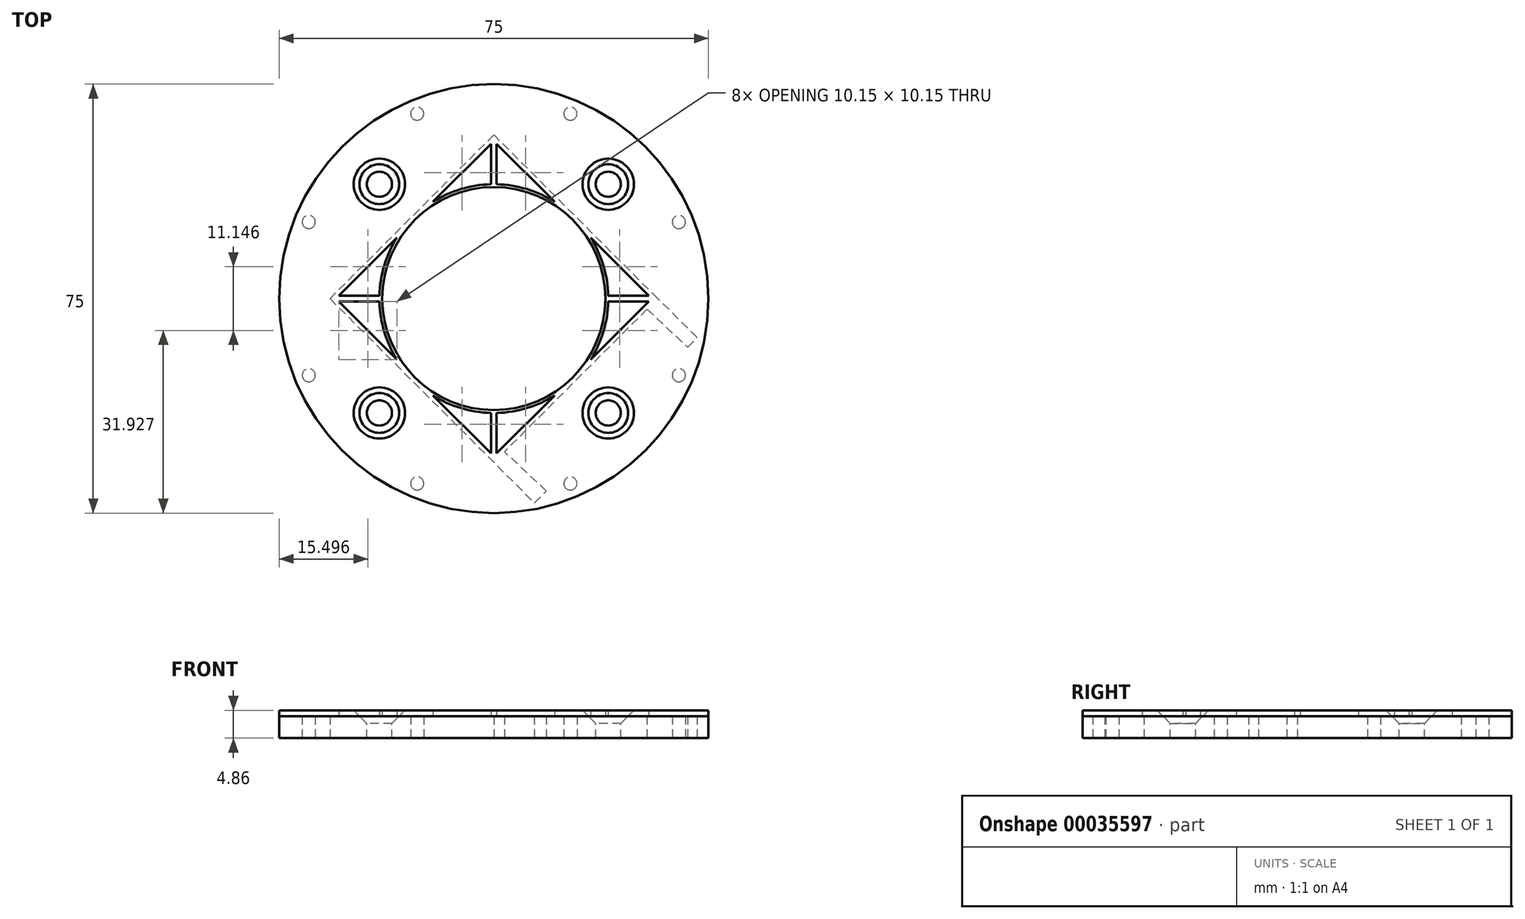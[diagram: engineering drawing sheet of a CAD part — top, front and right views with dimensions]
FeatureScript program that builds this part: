
annotation { "Feature Type Name" : "Feature", "Feature Type Description" : "" }
export const myFeature = defineFeature(function(context is Context, id is Id, definition is map)
    precondition{}
    {
        {
            var Q0;
            Q0=qCreatedBy(makeId("Top.planeOp"),FACE);
            var sketch = newSketch(context, id + "F0", { "sketchPlane" : qUnion([Q0])});
            skLineSegment(sketch, "E0.rect.bottom", {"start": v(20, -20) * mm, "end": v(-20, -20) * mm, "construction": true});
            skLineSegment(sketch, "E0.rect.top", {"start": v(20, 20) * mm, "end": v(-20, 20) * mm, "construction": true});
            skLineSegment(sketch, "E0.rect.left", {"start": v(20, -20) * mm, "end": v(20, 20) * mm, "construction": true});
            skPoint(sketch, "E0.rect.middle", {"position": v(0, 0) * mm});
            skLineSegment(sketch, "E1.bottom", {"start": v(26.79, -1.85) * mm, "end": v(1.86, -26.78) * mm});
            skLineSegment(sketch, "E1.left", {"start": v(28.64, 0) * mm, "end": v(0, 28.64) * mm});
            skLineSegment(sketch, "E1.right", {"start": v(0, -28.64) * mm, "end": v(-28.64, 0) * mm});
            skLineSegment(sketch, "E2", {"start": v(0, 28.64) * mm, "end": v(-28.64, 0) * mm});
            skCircle(sketch, "E3", {"center": v(0, 0) * mm, "radius": 37.5 * mm});
            skLineSegment(sketch, "E4", {"start": v(0, -28.64) * mm, "end": v(7.09, -35.72) * mm});
            skLineSegment(sketch, "E5", {"start": v(7.09, -35.72) * mm, "end": v(9.18, -33.63) * mm});
            skLineSegment(sketch, "E6", {"start": v(9.18, -33.63) * mm, "end": v(1.86, -26.78) * mm});
            skLineSegment(sketch, "E7", {"start": v(26.79, -1.85) * mm, "end": v(33.9, -8.51) * mm});
            skLineSegment(sketch, "E8", {"start": v(33.9, -8.51) * mm, "end": v(35.53, -6.77) * mm});
            skLineSegment(sketch, "E9", {"start": v(35.53, -6.77) * mm, "end": v(28.64, 0) * mm});
            skArc(sketch, "E10", {"start": v(6.24, -30.88) * mm, "mid": v(22.44, -22.1) * mm, "end": v(30.97, -5.77) * mm});
            skArc(sketch, "E11.trimOffspring", {"start": v(31.38, -2.7) * mm, "mid": v(-22.29, 22.26) * mm, "end": v(2.74, -31.38) * mm});
            skLineSegment(sketch, "E12", {"start": v(-20, -20) * mm, "end": v(-20, 20) * mm, "construction": true});
            skArc(sketch, "E13", {"start": v(5.87, -34.5) * mm, "mid": v(24.78, -24.72) * mm, "end": v(34.52, -5.78) * mm});
            skLineSegment(sketch, "E14", {"start": v(0, 0) * mm, "end": v(-40.64, 0) * mm, "construction": true});
            skLineSegment(sketch, "E15", {"start": v(-40.64, 0) * mm, "end": v(40.13, 0) * mm, "construction": true});
            skLineSegment(sketch, "E16", {"start": v(0, 0) * mm, "end": v(0, 39.12) * mm, "construction": true});
            skLineSegment(sketch, "E17", {"start": v(0, 0) * mm, "end": v(0, -39.38) * mm, "construction": true});
            skLineSegment(sketch, "E18", {"start": v(0, -39.38) * mm, "end": v(0, 0) * mm, "construction": true});
            skLineSegment(sketch, "E19", {"start": v(0, 0) * mm, "end": v(-39.64, 16.42) * mm, "construction": true});
            skLineSegment(sketch, "E20", {"start": v(0, 0) * mm, "end": v(-16.12, 38.93) * mm, "construction": true});
            skLineSegment(sketch, "E21", {"start": v(0, 0) * mm, "end": v(15.42, 37.24) * mm, "construction": true});
            skLineSegment(sketch, "E22", {"start": v(0, 0) * mm, "end": v(38.4, 15.9) * mm, "construction": true});
            skLineSegment(sketch, "E23", {"start": v(0, 0) * mm, "end": v(-37.76, -15.64) * mm, "construction": true});
            skLineSegment(sketch, "E24", {"start": v(0, 0) * mm, "end": v(-15.38, -37.13) * mm, "construction": true});
            skLineSegment(sketch, "E25", {"start": v(0, 0) * mm, "end": v(17.57, -42.41) * mm, "construction": true});
            skLineSegment(sketch, "E26", {"start": v(0, 0) * mm, "end": v(48.8, -20.21) * mm, "construction": true});
            skCircle(sketch, "E27", {"center": v(0, 0) * mm, "radius": 35 * mm, "construction": true});
            skPoint(sketch, "E28", {"position": v(-32.34, 13.4) * mm});
            skPoint(sketch, "E29", {"position": v(-13.4, 32.34) * mm});
            skPoint(sketch, "E30", {"position": v(13.4, 32.34) * mm});
            skPoint(sketch, "E31", {"position": v(32.34, 13.4) * mm});
            skPoint(sketch, "E32", {"position": v(32.34, -13.4) * mm});
            skPoint(sketch, "E33", {"position": v(13.4, -32.34) * mm});
            skPoint(sketch, "E34", {"position": v(-13.4, -32.34) * mm});
            skPoint(sketch, "E35", {"position": v(-32.34, -13.4) * mm});
            skSolve(sketch);
        }
        {
            var Q0;
            {var subQ1=sQuery(id+"F0.wireOp",EDGE,"63a967cb-fa63-414c-9bd4-498ef804fca7");Q0=makeQuery(id+"F0.imprint","IMPRINT",FACE,{"disambiguationData":[TD([[makeQuery(id+"F0.imprint","IMPRINT",EDGE,{"derivedFrom":subQ1}),1.0]])]});}
            var Q1;
            Q1=makeQuery(id+"F0.imprint","IMPRINT",FACE,{"disambiguationData":[TD([[makeQuery(id+"F0.imprint","IMPRINT",EDGE,{"derivedFrom":sQuery(id+"F0.wireOp",EDGE,"905c1fcb-210d-454b-8ad3-580b5945fc99")}),-1.0]])]});
            var Q2;
            Q2=makeQuery(id+"F0.imprint","IMPRINT",FACE,{"disambiguationData":[TD([[makeQuery(id+"F0.imprint","IMPRINT",EDGE,{"derivedFrom":sQuery(id+"F0.wireOp",EDGE,"42bf77fe-623c-47ce-9762-37b06fd64bbc")}),-1.0]])]});
            var Q3;
            {var subQ3=sQuery(id+"F0.wireOp",EDGE,"E1.left");Q3=makeQuery(id+"F0.imprint","IMPRINT",FACE,{"disambiguationData":[TD([[makeQuery(id+"F0.imprint","IMPRINT",EDGE,{"derivedFrom":subQ3}),-1.0]])]});}
            var Q4;
            {var subQ0=sQuery(id+"F0.wireOp",EDGE,"E1.bottom");Q4=makeQuery(id+"F0.imprint","IMPRINT",FACE,{"disambiguationData":[TD([[makeQuery(id+"F0.imprint","IMPRINT",EDGE,{"derivedFrom":subQ0}),1.0]])]});}
            var Q5;
            Q5=makeQuery(id+"F0.imprint","IMPRINT",FACE,{"disambiguationData":[TD([[makeQuery(id+"F0.imprint","IMPRINT",EDGE,{"derivedFrom":sQuery(id+"F0.wireOp",EDGE,"E3")}),1.0]])]});
            var Q6;
            {var subQ5=sQuery(id+"F0.wireOp",EDGE,"E10");Q6=makeQuery(id+"F0.imprint","IMPRINT",FACE,{"disambiguationData":[TD([[makeQuery(id+"F0.imprint","IMPRINT",EDGE,{"derivedFrom":subQ5}),-1.0]])]});}
            extrude(context, id + "F1", {"entities" : qUnion([Q0, Q1, Q2, Q3, Q4, Q5, Q6]), "depth" : 3.86 * mm});
        }
        {
            var Q0;
            Q0=makeQuery(id+"F1.opExtrude","CAP_FACE",FACE,{"disambiguationData":[OSD([sQuery(id+"F0.wireOp",EDGE,"42bf77fe-623c-47ce-9762-37b06fd64bbc"),sQuery(id+"F0.wireOp",EDGE,"80ae74b8-fb8b-4ab3-b5bb-8ff197e39af0"),sQuery(id+"F0.wireOp",EDGE,"c9e69175-ca6c-414e-95ab-96edb3b2d8ad"),sQuery(id+"F0.wireOp",EDGE,"E1.left"),sQuery(id+"F0.wireOp",EDGE,"E1.right"),sQuery(id+"F0.wireOp",EDGE,"E2"),sQuery(id+"F0.wireOp",EDGE,"vCClKhxT-Oz8s-tDXB-uJWS-lQwFzllClskl"),sQuery(id+"F0.wireOp",EDGE,"JmngBvq1-XjY0-KAw4-G1ba-JDdGeS6250UC"),sQuery(id+"F0.wireOp",EDGE,"7a4e4041-71b1-48b4-94f3-e571d922335e.trimOffspring")])],"isStart":false});
            var sketch = newSketch(context, id + "F2", { "sketchPlane" : qUnion([Q0])});
            skCircle(sketch, "E36", {"center": v(0, 0) * mm, "radius": 19.5 * mm});
            skCircle(sketch, "E37", {"center": v(0, 0) * mm, "radius": 37.5 * mm});
            skPoint(sketch, "E38.top.end.orphan", {"position": v(-39, 39) * mm});
            skPoint(sketch, "E38.left.end.orphan", {"position": v(39, 39) * mm});
            skPoint(sketch, "E38.bottom.end.orphan", {"position": v(-39, -39) * mm});
            skPoint(sketch, "E38.bottom.start.orphan", {"position": v(39, -39) * mm});
            skLineSegment(sketch, "E39.bottom", {"start": v(27.08, -0.5) * mm, "end": v(20, -0.5) * mm});
            skLineSegment(sketch, "E39.top", {"start": v(27.08, 0.5) * mm, "end": v(20, 0.5) * mm});
            skLineSegment(sketch, "E39.left", {"start": v(37.5, -0.5) * mm, "end": v(37.5, 0.5) * mm});
            skLineSegment(sketch, "E39.right", {"start": v(-37.5, -0.5) * mm, "end": v(-37.5, 0.5) * mm});
            skLineSegment(sketch, "E40.bottom", {"start": v(-0.5, -37.5) * mm, "end": v(0.5, -37.5) * mm});
            skLineSegment(sketch, "E40.top", {"start": v(-0.5, 37.5) * mm, "end": v(0.5, 37.5) * mm});
            skLineSegment(sketch, "E40.left", {"start": v(-0.5, -27.08) * mm, "end": v(-0.5, -20) * mm});
            skLineSegment(sketch, "E40.right", {"start": v(0.5, -27.08) * mm, "end": v(0.5, -20) * mm});
            skLineSegment(sketch, "E41.trimOffspring", {"start": v(-20, -0.5) * mm, "end": v(-27.08, -0.5) * mm});
            skLineSegment(sketch, "E42.trimOffspring", {"start": v(-20, 0.5) * mm, "end": v(-27.08, 0.5) * mm});
            skLineSegment(sketch, "E43.trimOffspring", {"start": v(-0.5, 20) * mm, "end": v(-0.5, 27.08) * mm});
            skLineSegment(sketch, "E44.trimOffspring", {"start": v(0.5, 20) * mm, "end": v(0.5, 27.08) * mm});
            skArc(sketch, "E45", {"start": v(-20, -0.5) * mm, "mid": v(-19.15, -5.78) * mm, "end": v(-16.93, -10.65) * mm});
            skArc(sketch, "E46.trimOffspring", {"start": v(0.5, -20) * mm, "mid": v(5.78, -19.15) * mm, "end": v(10.65, -16.93) * mm});
            skArc(sketch, "E47.trimOffspring", {"start": v(20, 0.5) * mm, "mid": v(19.15, 5.78) * mm, "end": v(16.93, 10.65) * mm});
            skArc(sketch, "E48.trimOffspring", {"start": v(-0.5, 20) * mm, "mid": v(-5.78, 19.15) * mm, "end": v(-10.65, 16.93) * mm});
            skLineSegment(sketch, "E49.bottom", {"start": v(27.08, -0.5) * mm, "end": v(0.5, -27.08) * mm});
            skLineSegment(sketch, "E49.top", {"start": v(-0.5, 27.08) * mm, "end": v(-27.08, 0.5) * mm});
            skLineSegment(sketch, "E49.left", {"start": v(27.08, 0.5) * mm, "end": v(0.5, 27.08) * mm});
            skLineSegment(sketch, "E49.right", {"start": v(-0.5, -27.08) * mm, "end": v(-27.08, -0.5) * mm});
            skArc(sketch, "E50.trimOffspring", {"start": v(-16.93, 10.65) * mm, "mid": v(-19.15, 5.78) * mm, "end": v(-20, 0.5) * mm});
            skArc(sketch, "E51.trimOffspring", {"start": v(10.65, 16.93) * mm, "mid": v(5.78, 19.15) * mm, "end": v(0.5, 20) * mm});
            skArc(sketch, "E52.trimOffspring", {"start": v(16.93, -10.65) * mm, "mid": v(19.15, -5.78) * mm, "end": v(20, -0.5) * mm});
            skArc(sketch, "E53.trimOffspring", {"start": v(-10.65, -16.93) * mm, "mid": v(-5.78, -19.15) * mm, "end": v(-0.5, -20) * mm});
            skSolve(sketch);
        }
        {
            var Q0;
            Q0 = qSketchRegion(id + "F2", true);
            extrude(context, id + "F3", {"entities" : qUnion([Q0]), "depth" : 1 * mm});
        }
        {
            var Q0;
            Q0=makeQuery(id+"F3.opExtrude","CAP_FACE",FACE,{"disambiguationData":[OSD([sQuery(id+"F2.wireOp",EDGE,"E36"),sQuery(id+"F2.wireOp",EDGE,"E37")])],"isStart":false});
            var sketch = newSketch(context, id + "F4", { "sketchPlane" : qUnion([Q0])});
            skLineSegment(sketch, "E54.bottom", {"start": v(20, -20) * mm, "end": v(-20, -20) * mm});
            skLineSegment(sketch, "E54.top", {"start": v(20, 20) * mm, "end": v(-20, 20) * mm});
            skLineSegment(sketch, "E54.left", {"start": v(20, -20) * mm, "end": v(20, 20) * mm});
            skLineSegment(sketch, "E54.right", {"start": v(-20, -20) * mm, "end": v(-20, 20) * mm});
            skPoint(sketch, "E54.middle", {"position": v(0, 0) * mm});
            skPoint(sketch, "E55", {"position": v(-40, 40) * mm});
            skPoint(sketch, "E56", {"position": v(40, 40) * mm});
            skPoint(sketch, "E57", {"position": v(40, -40) * mm});
            skPoint(sketch, "E58", {"position": v(-40, -40) * mm});
            skSolve(sketch);
        }
        {
            var Q0;
            Q0=sQuery(id+"F4.wireOp",VERTEX,"E54.right.start");
            var Q1;
            Q1=sQuery(id+"F4.wireOp",VERTEX,"E54.left.start");
            var Q2;
            Q2=sQuery(id+"F4.wireOp",VERTEX,"E54.top.start");
            var Q3;
            Q3=sQuery(id+"F4.wireOp",VERTEX,"E54.top.end");
            var Q4;
            Q4=makeQuery(id+"F1.opExtrude","SWEPT_BODY",BODY,{"disambiguationData":[OSD([sQuery(id+"F0.wireOp",EDGE,"E1.left"),sQuery(id+"F0.wireOp",EDGE,"E1.right"),sQuery(id+"F0.wireOp",EDGE,"E2"),sQuery(id+"F0.wireOp",EDGE,"vCClKhxT-Oz8s-tDXB-uJWS-lQwFzllClskl"),sQuery(id+"F0.wireOp",EDGE,"JmngBvq1-XjY0-KAw4-G1ba-JDdGeS6250UC"),sQuery(id+"F0.wireOp",EDGE,"7a4e4041-71b1-48b4-94f3-e571d922335e.trimOffspring")])]});
            var Q5;
            Q5=makeQuery(id+"F3.opExtrude","SWEPT_BODY",BODY,{"disambiguationData":[OSD([sQuery(id+"F2.wireOp",EDGE,"E36"),sQuery(id+"F2.wireOp",EDGE,"E37")])]});
            var Q6;
            Q6=makeQuery(id+"F1.opExtrude","SWEPT_BODY",BODY,{"disambiguationData":[OSD([sQuery(id+"F0.wireOp",EDGE,"63a967cb-fa63-414c-9bd4-498ef804fca7"),sQuery(id+"F0.wireOp",EDGE,"E1.bottom"),sQuery(id+"F0.wireOp",EDGE,"BehC58Ku-zQzz-ypBl-c1Vp-eOsnVaO1jlBa"),sQuery(id+"F0.wireOp",EDGE,"genWIfjl-CCSV-915T-R8z8-WEbJnyFzpU9r")])]});
            hole(context, id + "F5", {"style" : HoleStyle.C_SINK, "endStyle" : HoleEndStyle.BLIND, "standardTappedOrClearance" : lookupTablePath({ "standard" : "ISO", "fit" : "Normal", "size" : "M4", "type" : "Clearance" }), "standardBlindInLast" : lookupTablePath({ "fit" : "Standard", "standard" : "ISO", "size" : "M4", "type" : "Clearance" }), "holeDiameter" : 4.4 * mm, "cSinkDiameter" : 8.96 * mm, "cSinkAngle" : 90 * degree, "holeDepth" : 50 * mm, "startFromSketch" : true, "locations" : qUnion([Q0, Q1, Q2, Q3]), "scope" : qUnion([Q4, Q5, Q6])});
        }
        {
            var Q0;
            Q0=sQuery(id+"F0.wireOp",VERTEX,"E28");
            var Q1;
            Q1=sQuery(id+"F0.wireOp",VERTEX,"E29");
            var Q2;
            Q2=sQuery(id+"F0.wireOp",VERTEX,"E30");
            var Q3;
            Q3=sQuery(id+"F0.wireOp",VERTEX,"E31");
            var Q4;
            Q4=sQuery(id+"F0.wireOp",VERTEX,"E32");
            var Q5;
            Q5=sQuery(id+"F0.wireOp",VERTEX,"E33");
            var Q6;
            Q6=sQuery(id+"F0.wireOp",VERTEX,"E34");
            var Q7;
            Q7=sQuery(id+"F0.wireOp",VERTEX,"E35");
            var Q8;
            Q8=makeQuery(id+"F1.opExtrude","SWEPT_BODY",BODY,{"disambiguationData":[OSD([sQuery(id+"F0.wireOp",EDGE,"E1.left"),sQuery(id+"F0.wireOp",EDGE,"E1.right"),sQuery(id+"F0.wireOp",EDGE,"E2"),sQuery(id+"F0.wireOp",EDGE,"E3"),sQuery(id+"F0.wireOp",EDGE,"E4"),sQuery(id+"F0.wireOp",EDGE,"E5"),sQuery(id+"F0.wireOp",EDGE,"E8"),sQuery(id+"F0.wireOp",EDGE,"E9"),sQuery(id+"F0.wireOp",EDGE,"E13")])]});
            hole(context, id + "F6", {"style" : HoleStyle.SIMPLE, "endStyle" : HoleEndStyle.BLIND, "oppositeDirection" : true, "holeDiameter" : 2.3 * mm, "holeDepth" : 50 * mm, "locations" : qUnion([Q0, Q1, Q2, Q3, Q4, Q5, Q6, Q7]), "scope" : qUnion([Q8])});
        }
    });
